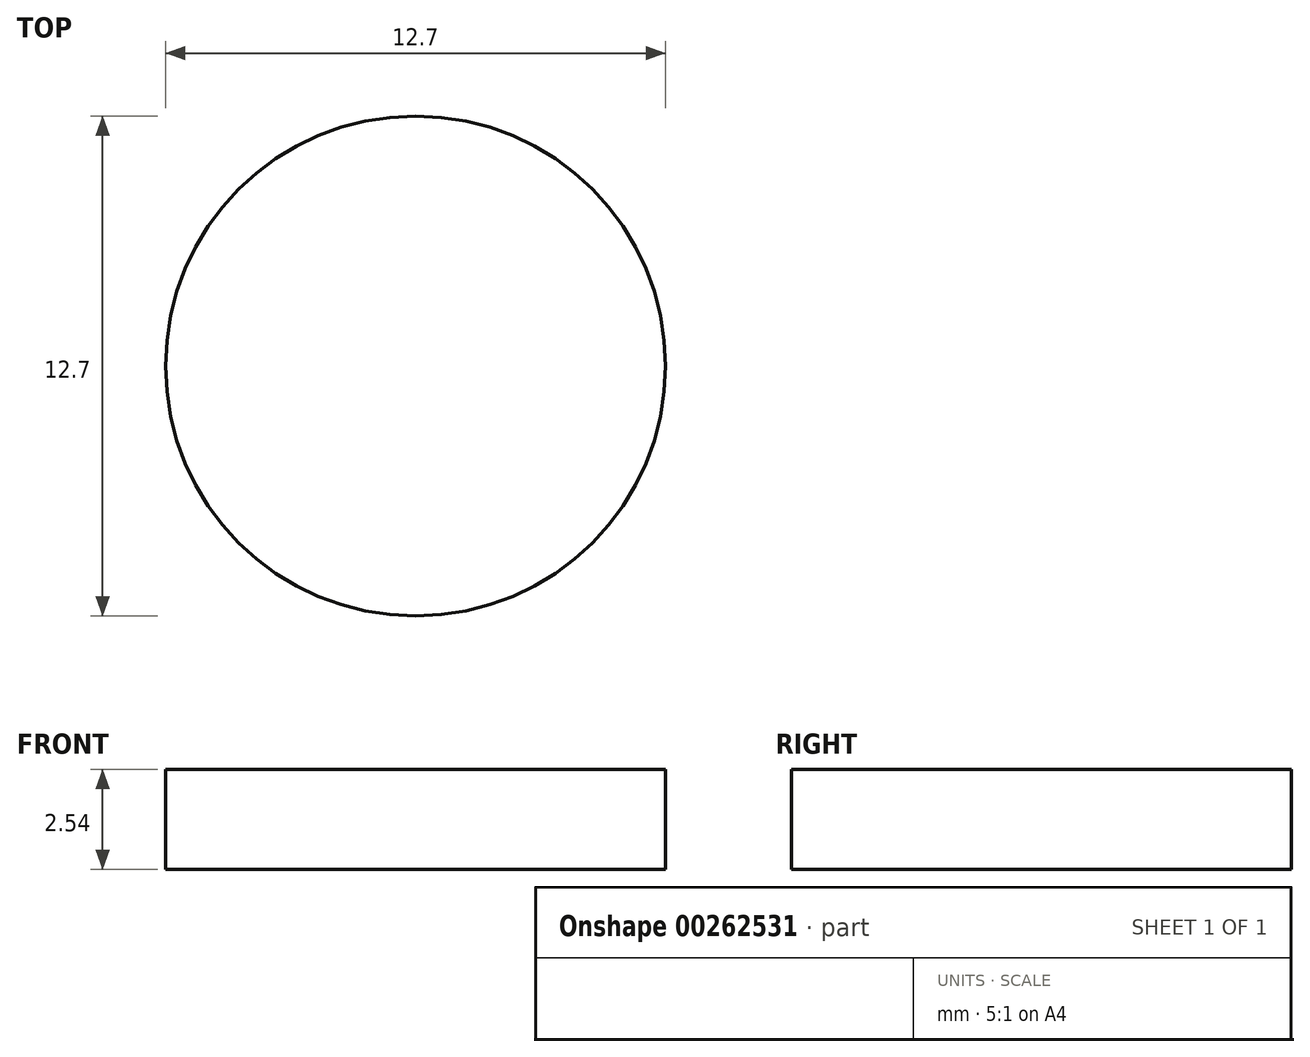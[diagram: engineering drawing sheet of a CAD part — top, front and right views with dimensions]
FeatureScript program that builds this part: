
annotation { "Feature Type Name" : "Feature", "Feature Type Description" : "" }
export const myFeature = defineFeature(function(context is Context, id is Id, definition is map)
    precondition{}
    {
        {
            var Q0;
            Q0=qCreatedBy(makeId("Top.planeOp"),FACE);
            var sketch = newSketch(context, id + "F0", { "sketchPlane" : qUnion([Q0])});
            skCircle(sketch, "E0", {"center": v(0, 0) * mm, "radius": 6.35 * mm});
            skSolve(sketch);
        }
        {
            var Q0;
            Q0=makeQuery(id+"F0.imprint","IMPRINT",FACE,{"disambiguationData":[TD([[makeQuery(id+"F0.imprint","IMPRINT",EDGE,{"derivedFrom":sQuery(id+"F0.wireOp",EDGE,"E0")}),1.0]])]});
            extrude(context, id + "F1", {"entities" : qUnion([Q0]), "depth" : 2.54 * mm});
        }
    });
